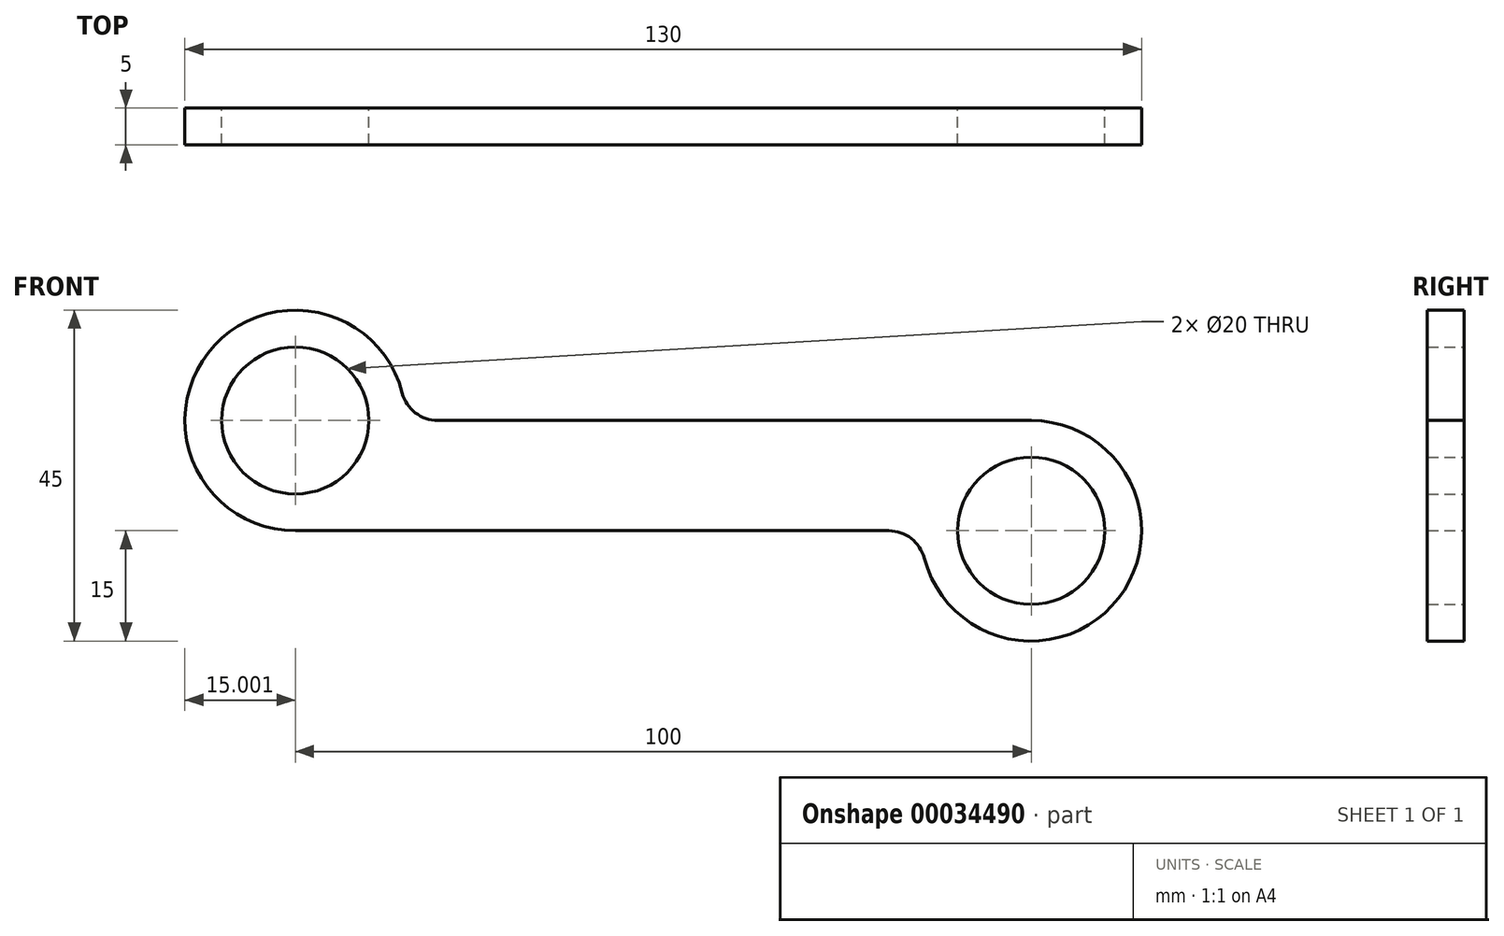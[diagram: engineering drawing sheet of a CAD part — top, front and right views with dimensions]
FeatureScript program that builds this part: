
annotation { "Feature Type Name" : "Feature", "Feature Type Description" : "" }
export const myFeature = defineFeature(function(context is Context, id is Id, definition is map)
    precondition{}
    {
        {
            var Q0;
            Q0=qCreatedBy(makeId("Front.planeOp"),FACE);
            var sketch = newSketch(context, id + "F0", { "sketchPlane" : qUnion([Q0])});
            skLineSegment(sketch, "E0.bottom", {"start": v(49.66, 15) * mm, "end": v(-50.34, 15) * mm});
            skLineSegment(sketch, "E0.top", {"start": v(49.66, 0) * mm, "end": v(-50.34, 0) * mm});
            skLineSegment(sketch, "E0.left", {"start": v(49.66, 15) * mm, "end": v(49.66, 0) * mm});
            skLineSegment(sketch, "E0.right", {"start": v(-50.34, 15) * mm, "end": v(-50.34, 0) * mm});
            skCircle(sketch, "E1", {"center": v(-50.34, 15) * mm, "radius": 15 * mm});
            skCircle(sketch, "E2", {"center": v(49.66, 0) * mm, "radius": 15 * mm});
            skCircle(sketch, "E3", {"center": v(-50.34, 15) * mm, "radius": 10 * mm});
            skCircle(sketch, "E4", {"center": v(49.66, 0) * mm, "radius": 10 * mm});
            skSolve(sketch);
        }
        {
            var Q0;
            {var subQ3=sQuery(id+"F0.wireOp",EDGE,"E0.bottom");var subQ5=sQuery(id+"F0.wireOp",EDGE,"E1");var subQ7=makeQuery(id+"F0.imprint","INTERSECT",VERTEX,{"derivedFrom":[subQ3,subQ5]});Q0=makeQuery(id+"F0.imprint","IMPRINT",FACE,{"disambiguationData":[TD([[makeQuery(id+"F0.imprint","IMPRINT",EDGE,{"disambiguationData":[TD([[subQ7,-1.0]])],"derivedFrom":subQ3}),-1.0]])]});}
            var Q1;
            {var subQ1=sQuery(id+"F0.wireOp",EDGE,"E0.left");var subQ8=sQuery(id+"F0.wireOp",EDGE,"E0.bottom");var subQ11=makeQuery(id+"F0.imprint","INTERSECT",VERTEX,{"derivedFrom":[subQ8,subQ1]});Q1=makeQuery(id+"F0.imprint","IMPRINT",FACE,{"disambiguationData":[TD([[makeQuery(id+"F0.imprint","IMPRINT",EDGE,{"disambiguationData":[TD([[subQ11,-1.0]])],"derivedFrom":subQ8}),1.0]])]});}
            var Q2;
            {var subQ0=sQuery(id+"F0.wireOp",EDGE,"E1");var subQ3=sQuery(id+"F0.wireOp",EDGE,"E0.bottom");var subQ4=makeQuery(id+"F0.imprint","INTERSECT",VERTEX,{"derivedFrom":[subQ3,subQ0]});Q2=makeQuery(id+"F0.imprint","IMPRINT",FACE,{"disambiguationData":[TD([[makeQuery(id+"F0.imprint","IMPRINT",EDGE,{"disambiguationData":[TD([[subQ4,-1.0]])],"derivedFrom":subQ3}),1.0]])]});}
            var Q3;
            {var subQ3=sQuery(id+"F0.wireOp",EDGE,"E0.top");var subQ5=sQuery(id+"F0.wireOp",EDGE,"E2");var subQ7=makeQuery(id+"F0.imprint","INTERSECT",VERTEX,{"derivedFrom":[subQ3,subQ5]});Q3=makeQuery(id+"F0.imprint","IMPRINT",FACE,{"disambiguationData":[TD([[makeQuery(id+"F0.imprint","IMPRINT",EDGE,{"disambiguationData":[TD([[subQ7,1.0]])],"derivedFrom":subQ3}),1.0]])]});}
            var Q4;
            {var subQ3=sQuery(id+"F0.wireOp",EDGE,"E0.top");var subQ5=sQuery(id+"F0.wireOp",EDGE,"E2");var subQ7=makeQuery(id+"F0.imprint","INTERSECT",VERTEX,{"derivedFrom":[subQ3,subQ5]});Q4=makeQuery(id+"F0.imprint","IMPRINT",FACE,{"disambiguationData":[TD([[makeQuery(id+"F0.imprint","IMPRINT",EDGE,{"disambiguationData":[TD([[subQ7,1.0]])],"derivedFrom":subQ3}),-1.0]])]});}
            extrude(context, id + "F1", {"entities" : qUnion([Q0, Q1, Q2, Q3, Q4]), "depth" : 5 * mm});
        }
        {
            var Q0;
            Q0=makeQuery(id+"F1.opExtrude","SWEPT_EDGE",EDGE,{"disambiguationData":[OSD([sQuery(id+"F0.wireOp",EDGE,"E0.bottom"),sQuery(id+"F0.wireOp",EDGE,"E1")])]});
            var Q1;
            Q1=makeQuery(id+"F1.opExtrude","SWEPT_EDGE",EDGE,{"disambiguationData":[OSD([sQuery(id+"F0.wireOp",EDGE,"E0.top"),sQuery(id+"F0.wireOp",EDGE,"E2")])]});
            fillet(context, id + "F2", {"entities" : qUnion([Q0, Q1]), "radius" : 5 * mm, "tangentPropagation" : true, "allowEdgeOverflow" : false});
        }
    });
